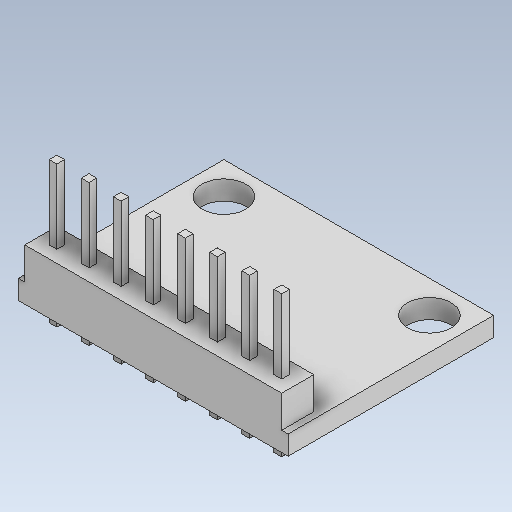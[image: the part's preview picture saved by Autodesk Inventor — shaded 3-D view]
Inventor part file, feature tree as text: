
AUTODESK INVENTOR PART (.ipt)
format: ipt  version: 2020.2 (Build 242310000, 310)  size: 211,456 bytes
history: native  units: mm
features: sketch x4, extrude x3, hole x1
ambient origin geometry x8: Origin, YZ Plane, XZ Plane, XY Plane, X Axis, Y Axis, Z Axis, Center Point
bodies: Solido1 (feature_tree)
feature tree (8):
  extrude  "Estrusione1"  Depth=16.0mm
  hole  "Foro1"  [1 undecoded]
  extrude  "Estrusione2"  Depth=1.5mm TaperAngle=0.0deg
  extrude  "Estrusione3"  Depth=2.5mm
  sketch  "Schizzo1"
  sketch  "Schizzo2"
  sketch  "Schizzo4"
  sketch  "Schizzo6"
note: 1 required parameter value undecoded (feature->parameter linkage not recoverable at this tier; creation-order binding heuristic only, values carry confidence <= 0.55)
